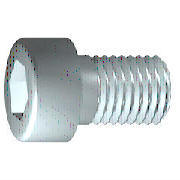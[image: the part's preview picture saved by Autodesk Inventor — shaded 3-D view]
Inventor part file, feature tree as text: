
AUTODESK INVENTOR PART (.ipt)
format: ipt  version: 2022 (Build 260153000, 153)  size: 187,904 bytes
history: native  units: mm (DEFAULTED — no unit token found)
features: sketch x2, other x1, extrude x1, plane x1, fillet x1
ambient origin geometry x7: Origin, YZ Plane, XY Plane, X Axis, Y Axis, Z Axis, Center Point
bodies: Solid1 (feature_tree)
feature tree (6):
  other  "Базовый элемент"
  extrude  "Паз"  Depth=20.0mm
  plane  "Work Plane1"
  fillet  "Fillet2"  Radius=0.429515mm
  sketch  "Эскиз1"
  sketch  "Эскиз2"
